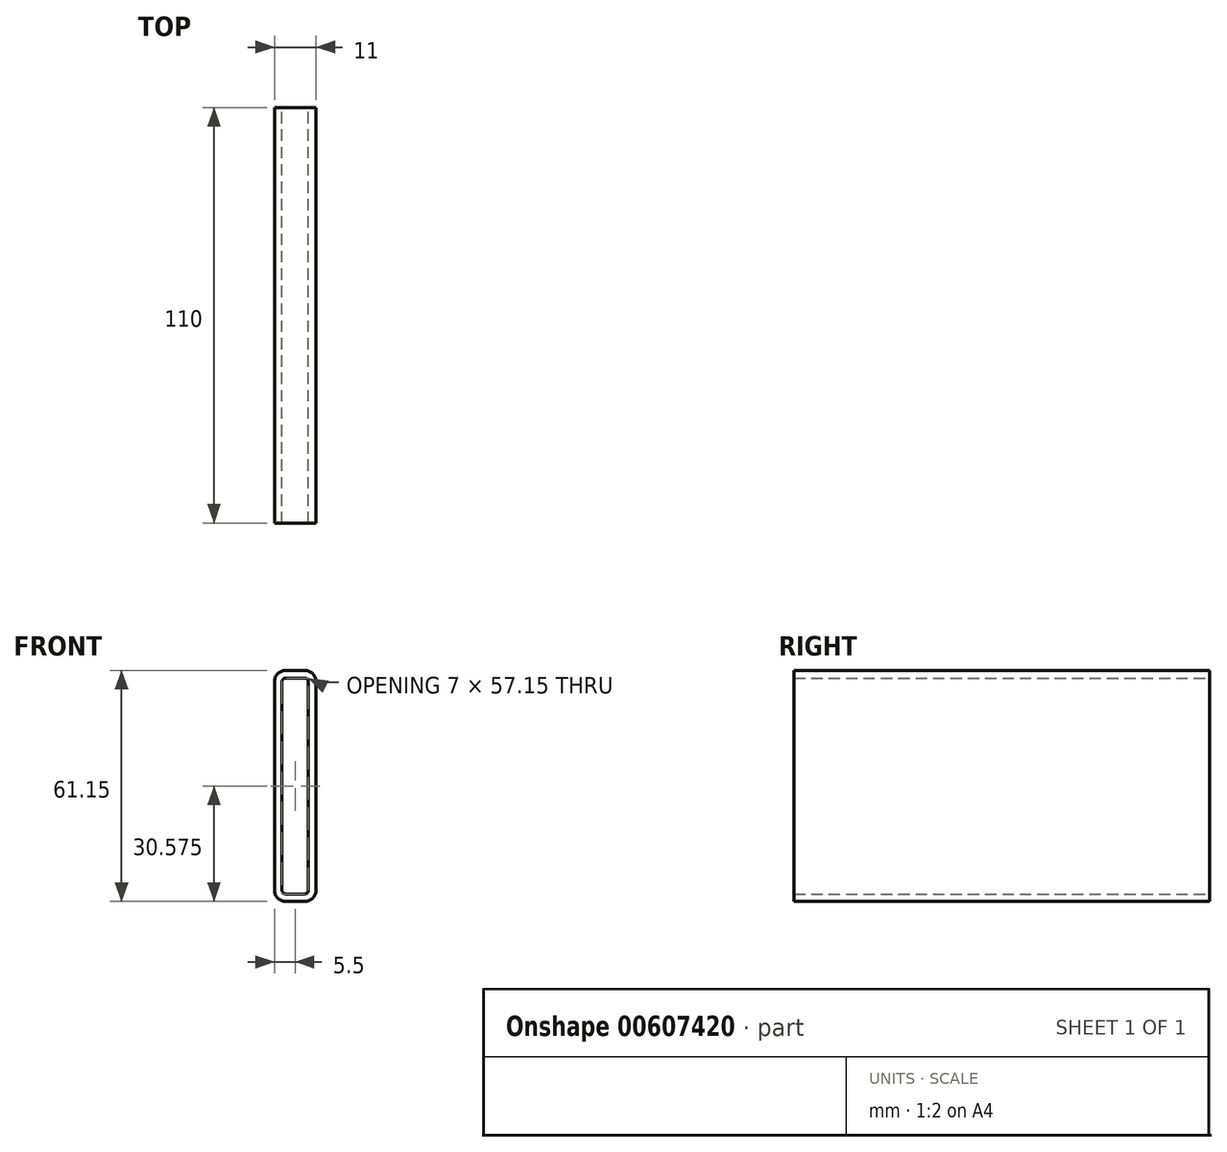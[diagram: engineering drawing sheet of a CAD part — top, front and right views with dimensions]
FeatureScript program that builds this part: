
annotation { "Feature Type Name" : "Feature", "Feature Type Description" : "" }
export const myFeature = defineFeature(function(context is Context, id is Id, definition is map)
    precondition{}
    {
        {
            var Q0;
            Q0=qCreatedBy(makeId("Front.planeOp"),FACE);
            var sketch = newSketch(context, id + "F0", { "sketchPlane" : qUnion([Q0])});
            skLineSegment(sketch, "E0.bottom", {"start": v(1, 0) * mm, "end": v(6, 0) * mm});
            skLineSegment(sketch, "E0.top", {"start": v(1, 57.15) * mm, "end": v(6, 57.15) * mm});
            skLineSegment(sketch, "E0.left", {"start": v(0, 1) * mm, "end": v(0, 56.15) * mm});
            skLineSegment(sketch, "E0.right", {"start": v(7, 1) * mm, "end": v(7, 56.15) * mm});
            skPoint(sketch, "E1.visualSharp", {"position": v(7, 0) * mm});
            skArc(sketch, "E1.filletArc", {"start": v(6, 0) * mm, "mid": v(6.7, 0.3) * mm, "end": v(7, 1) * mm});
            skPoint(sketch, "E2.visualSharp", {"position": v(7, 57.15) * mm});
            skArc(sketch, "E2.filletArc", {"start": v(7, 56.15) * mm, "mid": v(6.7, 56.86) * mm, "end": v(6, 57.15) * mm});
            skPoint(sketch, "E3.visualSharp", {"position": v(0, 57.15) * mm});
            skArc(sketch, "E3.filletArc", {"start": v(1, 57.15) * mm, "mid": v(0.3, 56.86) * mm, "end": v(0, 56.15) * mm});
            skPoint(sketch, "E4.visualSharp", {"position": v(0, 0) * mm});
            skArc(sketch, "E4.filletArc", {"start": v(0, 1) * mm, "mid": v(0.3, 0.3) * mm, "end": v(1, 0) * mm});
            skArc(sketch, "E5.0", {"start": v(6, -2) * mm, "mid": v(8.12, -1.12) * mm, "end": v(9, 1) * mm});
            skLineSegment(sketch, "E5.1", {"start": v(1, -2) * mm, "end": v(6, -2) * mm});
            skLineSegment(sketch, "E5.2", {"start": v(9, 1) * mm, "end": v(9, 56.15) * mm});
            skArc(sketch, "E5.3", {"start": v(-2, 1) * mm, "mid": v(-1.12, -1.12) * mm, "end": v(1, -2) * mm});
            skArc(sketch, "E5.4", {"start": v(9, 56.15) * mm, "mid": v(8.12, 58.27) * mm, "end": v(6, 59.15) * mm});
            skLineSegment(sketch, "E5.5", {"start": v(1, 59.15) * mm, "end": v(6, 59.15) * mm});
            skArc(sketch, "E5.6", {"start": v(1, 59.15) * mm, "mid": v(-1.12, 58.27) * mm, "end": v(-2, 56.15) * mm});
            skLineSegment(sketch, "E5.7", {"start": v(-2, 1) * mm, "end": v(-2, 56.15) * mm});
            skSolve(sketch);
        }
        {
            var Q0;
            Q0=makeQuery(id+"F0.imprint","IMPRINT",FACE,{"disambiguationData":[TD([[makeQuery(id+"F0.imprint","IMPRINT",EDGE,{"derivedFrom":sQuery(id+"F0.wireOp",EDGE,"E0.bottom")}),-1.0]])]});
            extrude(context, id + "F1", {"entities" : qUnion([Q0]), "depth" : 110 * mm, "offsetDistance" : 25 * mm});
        }
    });
